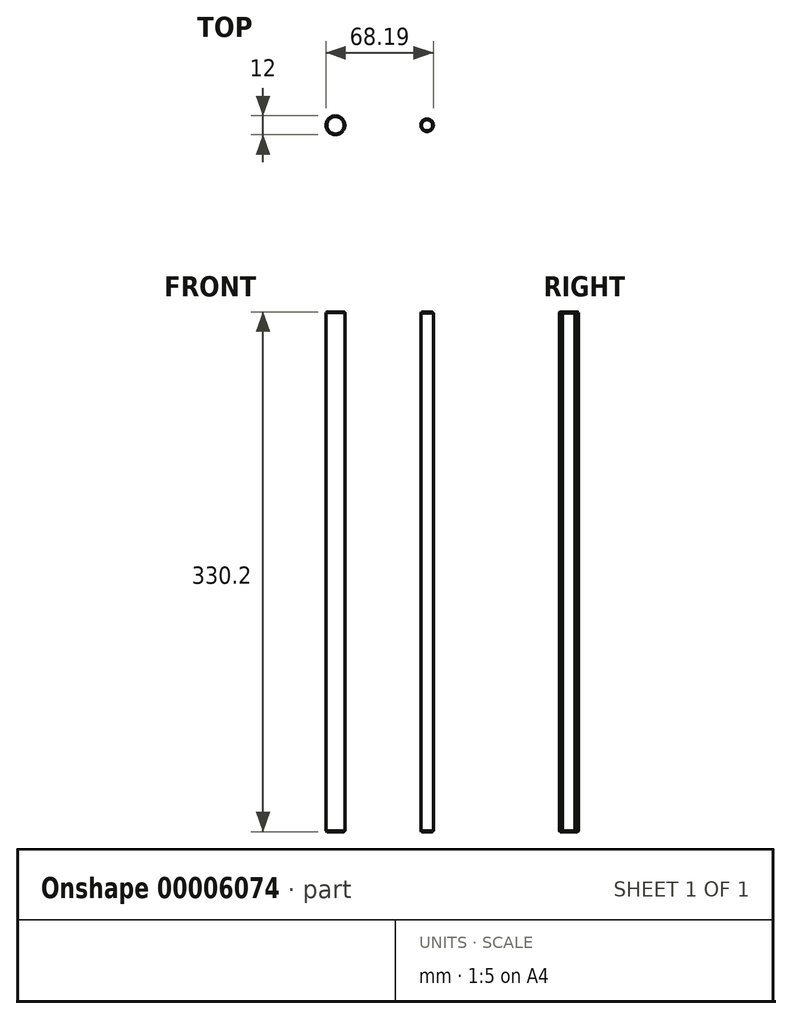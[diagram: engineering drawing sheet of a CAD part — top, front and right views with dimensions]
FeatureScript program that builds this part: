
annotation { "Feature Type Name" : "Feature", "Feature Type Description" : "" }
export const myFeature = defineFeature(function(context is Context, id is Id, definition is map)
    precondition{}
    {
        {
            var Q0;
            Q0=qCreatedBy(makeId("Top.planeOp"),FACE);
            var sketch = newSketch(context, id + "F0", { "sketchPlane" : qUnion([Q0])});
            skCircle(sketch, "E0", {"center": v(0, 0) * mm, "radius": 6 * mm});
            skLineSegment(sketch, "E1", {"start": v(0, 0) * mm, "end": v(58.19, 0) * mm, "construction": true});
            skCircle(sketch, "E2", {"center": v(58.19, 0) * mm, "radius": 4 * mm});
            skSolve(sketch);
        }
        {
            var Q0;
            Q0=makeQuery(id+"F0.imprint","IMPRINT",FACE,{"disambiguationData":[TD([[makeQuery(id+"F0.imprint","IMPRINT",EDGE,{"derivedFrom":sQuery(id+"F0.wireOp",EDGE,"E0")}),1.0]])]});
            extrude(context, id + "F1", {"entities" : qUnion([Q0]), "depth" : 330.2 * mm});
        }
        {
            var Q0;
            Q0=makeQuery(id+"F0.imprint","IMPRINT",FACE,{"disambiguationData":[TD([[makeQuery(id+"F0.imprint","IMPRINT",EDGE,{"derivedFrom":sQuery(id+"F0.wireOp",EDGE,"E2")}),1.0]])]});
            extrude(context, id + "F2", {"entities" : qUnion([Q0]), "depth" : 330 * mm});
        }
        {
            var Q0;
            Q0=makeQuery(id+"F1.opExtrude","CAP_EDGE",EDGE,{"disambiguationData":[OSD([sQuery(id+"F0.wireOp",EDGE,"E0")])],"isStart":false});
            var Q1;
            Q1=makeQuery(id+"F1.opExtrude","CAP_EDGE",EDGE,{"disambiguationData":[OSD([sQuery(id+"F0.wireOp",EDGE,"E0")])],"isStart":true});
            var Q2;
            Q2=makeQuery(id+"F2.opExtrude","CAP_EDGE",EDGE,{"disambiguationData":[OSD([sQuery(id+"F0.wireOp",EDGE,"E2")])],"isStart":true});
            var Q3;
            Q3=makeQuery(id+"F2.opExtrude","CAP_EDGE",EDGE,{"disambiguationData":[OSD([sQuery(id+"F0.wireOp",EDGE,"E2")])],"isStart":false});
            chamfer(context, id + "F3", {"entities" : qUnion([Q0, Q1, Q2, Q3]), "width" : 0.5 * mm, "tangentPropagation" : true});
        }
    });
